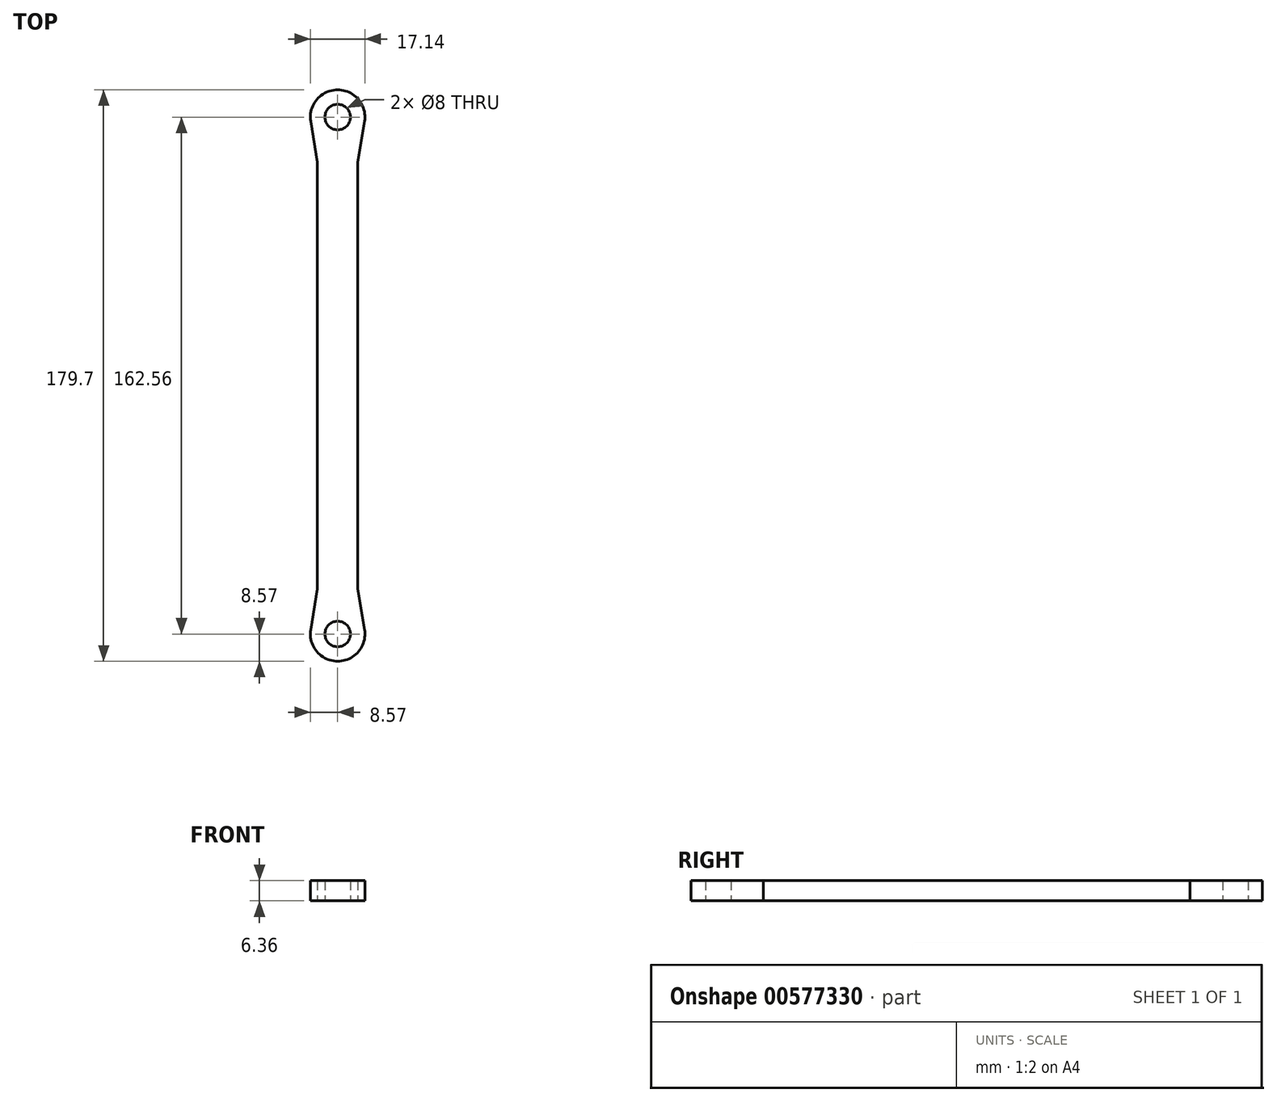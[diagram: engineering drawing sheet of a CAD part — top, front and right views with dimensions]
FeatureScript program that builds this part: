
annotation { "Feature Type Name" : "Feature", "Feature Type Description" : "" }
export const myFeature = defineFeature(function(context is Context, id is Id, definition is map)
    precondition{}
    {
        {
            var Q0;
            Q0=qCreatedBy(makeId("Top.planeOp"),FACE);
            var sketch = newSketch(context, id + "F0", { "sketchPlane" : qUnion([Q0])});
            skArc(sketch, "E0", {"start": v(0, -85.28) * mm, "mid": v(4, -81.28) * mm, "end": v(0, -77.28) * mm});
            skArc(sketch, "E1", {"start": v(0, -89.85) * mm, "mid": v(6.53, -86.83) * mm, "end": v(8.46, -79.89) * mm});
            skLineSegment(sketch, "E2", {"start": v(0, 0) * mm, "end": v(6.35, 0) * mm});
            skLineSegment(sketch, "E3", {"start": v(6.35, 0) * mm, "end": v(6.35, -67.06) * mm});
            skLineSegment(sketch, "E4", {"start": v(6.35, -67.06) * mm, "end": v(8.46, -79.89) * mm});
            skLineSegment(sketch, "E5", {"start": v(0, -89.85) * mm, "end": v(0, -85.28) * mm});
            skLineSegment(sketch, "E6.trimOffspring", {"start": v(0, -77.28) * mm, "end": v(0, 0) * mm});
            skSolve(sketch);
        }
        {
            var Q0;
            Q0 = qSketchRegion(id + "F0", true);
            extrude(context, id + "F1", {"entities" : qUnion([Q0]), "endBound" : BoundingType.SYMMETRIC, "depth" : 6.35 * mm, "offsetDistance" : 25.4 * mm});
        }
        {
            var Q0;
            Q0=makeQuery(id+"F1.opExtrude","SWEPT_BODY",BODY,{"disambiguationData":[OSD([sQuery(id+"F0.wireOp",EDGE,"E0"),sQuery(id+"F0.wireOp",EDGE,"E1"),sQuery(id+"F0.wireOp",EDGE,"E2"),sQuery(id+"F0.wireOp",EDGE,"E3"),sQuery(id+"F0.wireOp",EDGE,"E4"),sQuery(id+"F0.wireOp",EDGE,"E5"),sQuery(id+"F0.wireOp",EDGE,"E6.trimOffspring")])]});
            var Q1;
            Q1=qCreatedBy(makeId("Right.planeOp"),FACE);
            mirror(context, id + "F2", {"operationType" : NewBodyOperationType.ADD, "entities" : qUnion([Q0]), "mirrorPlane" : qUnion([Q1])});
        }
        {
            var Q0;
            Q0=makeQuery(id+"F1.opExtrude","SWEPT_BODY",BODY,{"disambiguationData":[OSD([sQuery(id+"F0.wireOp",EDGE,"E0"),sQuery(id+"F0.wireOp",EDGE,"E1"),sQuery(id+"F0.wireOp",EDGE,"E2"),sQuery(id+"F0.wireOp",EDGE,"E3"),sQuery(id+"F0.wireOp",EDGE,"E4"),sQuery(id+"F0.wireOp",EDGE,"E5"),sQuery(id+"F0.wireOp",EDGE,"E6.trimOffspring")])]});
            var Q1;
            Q1=qCreatedBy(makeId("Front.planeOp"),FACE);
            mirror(context, id + "F3", {"operationType" : NewBodyOperationType.ADD, "entities" : qUnion([Q0]), "mirrorPlane" : qUnion([Q1])});
        }
    });
